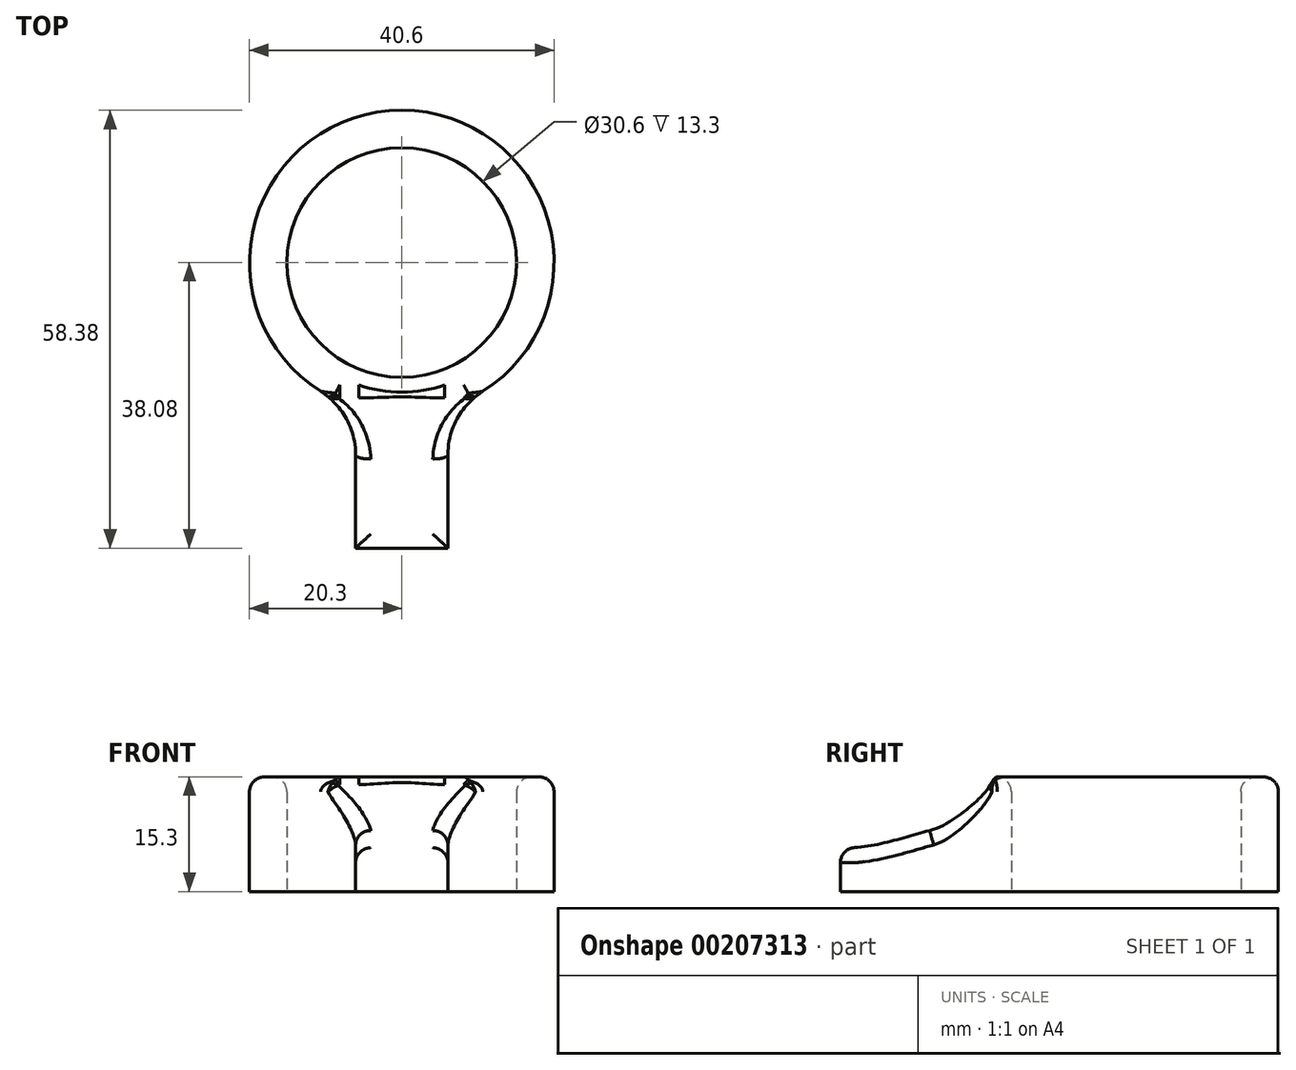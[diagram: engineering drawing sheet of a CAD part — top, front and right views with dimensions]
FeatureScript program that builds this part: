
annotation { "Feature Type Name" : "Feature", "Feature Type Description" : "" }
export const myFeature = defineFeature(function(context is Context, id is Id, definition is map)
    precondition{}
    {
        {
            var Q0;
            Q0=qCreatedBy(makeId("Top.planeOp"),FACE);
            var sketch = newSketch(context, id + "F0", { "sketchPlane" : qUnion([Q0])});
            skCircle(sketch, "E0.0", {"center": v(0, 0) * mm, "radius": 15.3 * mm});
            skArc(sketch, "E1.0", {"start": v(6.15, -19.35) * mm, "mid": v(0, 20.3) * mm, "end": v(-6.15, -19.35) * mm});
            skLineSegment(sketch, "E2", {"start": v(6.15, -38.08) * mm, "end": v(6.15, -24.74) * mm});
            skLineSegment(sketch, "E3", {"start": v(-6.15, -24.43) * mm, "end": v(-6.15, -38.08) * mm});
            skLineSegment(sketch, "E4", {"start": v(6.15, -24.74) * mm, "end": v(6.15, -19.35) * mm});
            skLineSegment(sketch, "E5", {"start": v(-6.15, -24.43) * mm, "end": v(-6.15, -19.35) * mm});
            skLineSegment(sketch, "E6", {"start": v(-6.15, -38.08) * mm, "end": v(6.15, -38.08) * mm});
            skSolve(sketch);
        }
        {
            var Q0;
            Q0=makeQuery(id+"F0.imprint","IMPRINT",FACE,{"disambiguationData":[TD([[makeQuery(id+"F0.imprint","IMPRINT",EDGE,{"derivedFrom":sQuery(id+"F0.wireOp",EDGE,"E0.0")}),-1.0]])]});
            extrude(context, id + "F1", {"entities" : qUnion([Q0]), "depth" : 15.3 * mm});
        }
        {
            var Q0;
            Q0=makeQuery(id+"F1.opExtrude","CAP_EDGE",EDGE,{"disambiguationData":[OSD([sQuery(id+"F0.wireOp",EDGE,"E0.0")])],"isStart":false});
            var Q1;
            Q1=makeQuery(id+"F1.opExtrude","CAP_EDGE",EDGE,{"disambiguationData":[OSD([sQuery(id+"F0.wireOp",EDGE,"E1.0")])],"isStart":false});
            fillet(context, id + "F2", {"entities" : qUnion([Q0, Q1]), "radius" : 2 * mm, "tangentPropagation" : true, "allowEdgeOverflow" : false});
        }
        {
            var Q0;
            Q0=makeQuery(id+"F1.opExtrude","CAP_EDGE",EDGE,{"disambiguationData":[OSD([sQuery(id+"F0.wireOp",EDGE,"E2"),sQuery(id+"F0.wireOp",EDGE,"E4")])],"isStart":false});
            var Q1;
            Q1=makeQuery(id+"F1.opExtrude","CAP_EDGE",EDGE,{"disambiguationData":[OSD([sQuery(id+"F0.wireOp",EDGE,"E3"),sQuery(id+"F0.wireOp",EDGE,"E5")])],"isStart":false});
            fillet(context, id + "F3", {"entities" : qUnion([Q0, Q1]), "radius" : 2 * mm, "tangentPropagation" : true, "allowEdgeOverflow" : false});
        }
        {
            var Q0;
            Q0=makeQuery(id+"F1.opExtrude","SWEPT_EDGE",EDGE,{"disambiguationData":[OSD([sQuery(id+"F0.wireOp",EDGE,"E1.0"),sQuery(id+"F0.wireOp",EDGE,"E4")])]});
            fillet(context, id + "F4", {"entities" : qUnion([Q0]), "radius" : 10 * mm, "tangentPropagation" : true, "allowEdgeOverflow" : false});
        }
        {
            var Q0;
            Q0=makeQuery(id+"F1.opExtrude","SWEPT_EDGE",EDGE,{"disambiguationData":[OSD([sQuery(id+"F0.wireOp",EDGE,"E1.0"),sQuery(id+"F0.wireOp",EDGE,"E5")])]});
            fillet(context, id + "F5", {"entities" : qUnion([Q0]), "radius" : 10 * mm, "tangentPropagation" : true, "allowEdgeOverflow" : false});
        }
        {
            var Q0;
            Q0=qCreatedBy(makeId("Right.planeOp"),FACE);
            var sketch = newSketch(context, id + "F6", { "sketchPlane" : qUnion([Q0])});
            skFitSpline(sketch, "E7", {"points": [v(-40.56, 6.7) * mm, v(-27.77, 7.7) * mm, v(-23.25, 9.5) * mm, v(-17.72, 15.9) * mm, v(-32.45, 18.39) * mm, v(-40.95, 15.35) * mm, v(-40.56, 6.7) * mm]});
            skSolve(sketch);
        }
        {
            var Q0;
            Q0=makeQuery(id+"F6.imprint","IMPRINT",FACE,{"disambiguationData":[TD([[makeQuery(id+"F6.imprint","IMPRINT",EDGE,{"derivedFrom":sQuery(id+"F6.wireOp",EDGE,"E7")}),1.0]])]});
            extrude(context, id + "F7", {"entities" : qUnion([Q0]), "operationType" : NewBodyOperationType.REMOVE, "endBound" : BoundingType.SYMMETRIC, "depth" : 25 * mm});
        }
        {
            var Q0;
            Q0=makeQuery(id+"F7.boolean.opBoolean","COPY",FACE,{"derivedFrom":makeQuery(id+"F7.opExtrude","SWEPT_FACE",FACE,{"disambiguationData":[OSD([sQuery(id+"F6.wireOp",EDGE,"E7")])]})});
            fillet(context, id + "F8", {"entities" : qUnion([Q0]), "radius" : 2 * mm, "tangentPropagation" : true, "allowEdgeOverflow" : false});
        }
    });
